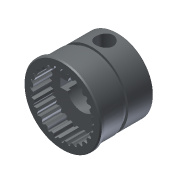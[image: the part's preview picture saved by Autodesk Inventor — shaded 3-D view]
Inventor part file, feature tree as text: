
AUTODESK INVENTOR PART (.ipt)
format: ipt  version: 2013 (Build 170138000, 138)  size: 330,240 bytes
history: native  units: in
note: dims shown in document units (in); Inventor stores cm internally (conversion verified against a paired STEP export)
features: fillet x1, other x1, imported_body x1
ambient origin geometry x8: Origin, YZ Plane, XZ Plane, XY Plane, X Axis, Y Axis, Z Axis, Center Point
feature tree (3):
  fillet  "Fillet1"  [1 undecoded]
  other  "217-2625-009 Rev11"
  imported_body  "Base1"
note: 1 required parameter value undecoded (feature->parameter linkage not recoverable at this tier; creation-order binding heuristic only, values carry confidence <= 0.55)
